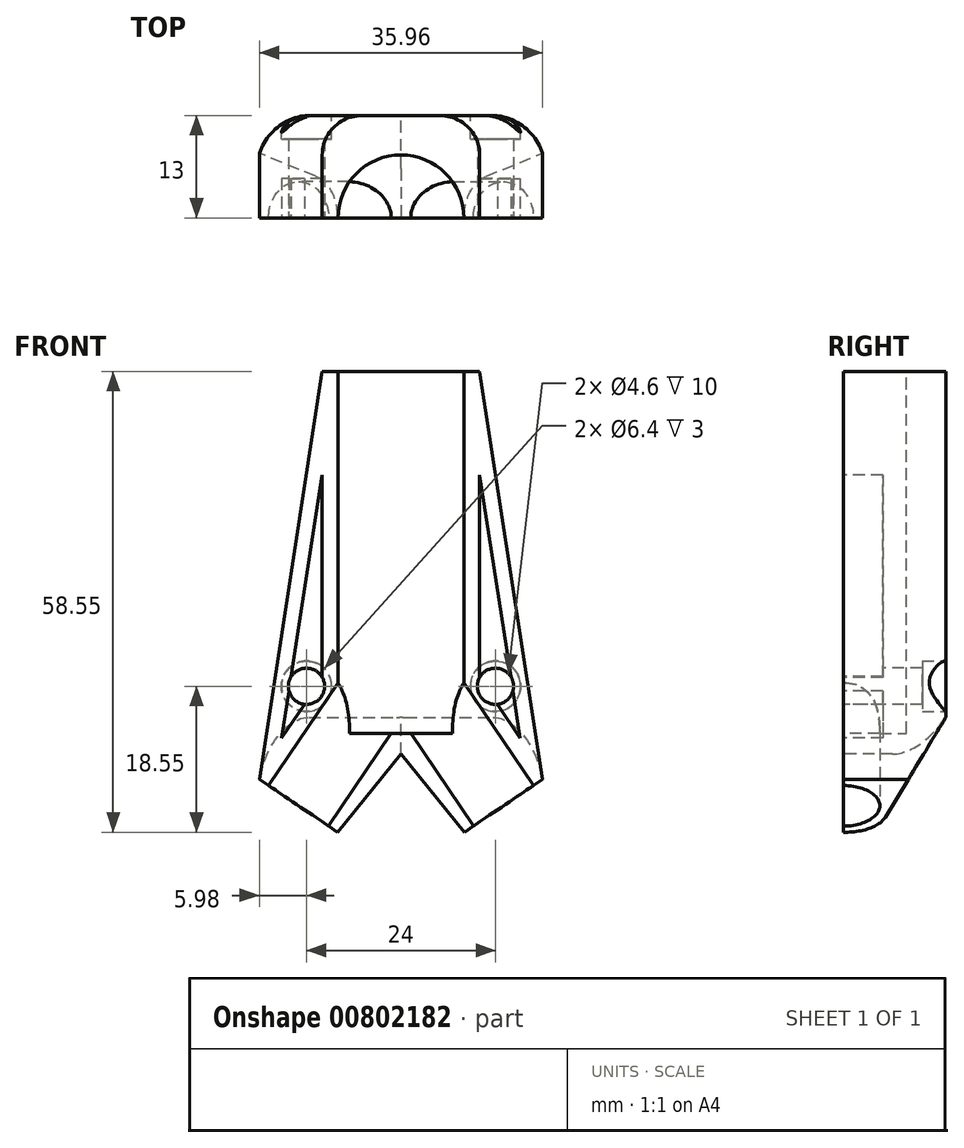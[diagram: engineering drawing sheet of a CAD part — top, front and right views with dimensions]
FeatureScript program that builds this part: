
annotation { "Feature Type Name" : "Feature", "Feature Type Description" : "" }
export const myFeature = defineFeature(function(context is Context, id is Id, definition is map)
    precondition{}
    {
        {
            var Q0;
            Q0=qCreatedBy(makeId("Front.planeOp"),FACE);
            var sketch = newSketch(context, id + "F0", { "sketchPlane" : qUnion([Q0])});
            skLineSegment(sketch, "E0", {"start": v(0, 0) * mm, "end": v(0, 0) * mm});
            skLineSegment(sketch, "E1.bottom", {"start": v(-10, 40) * mm, "end": v(10, 40) * mm});
            skLineSegment(sketch, "E2", {"start": v(0, -8.61) * mm, "end": v(-8.04, -18.55) * mm});
            skLineSegment(sketch, "E3", {"start": v(-8.04, -18.55) * mm, "end": v(-17.98, -11.83) * mm});
            skLineSegment(sketch, "E4", {"start": v(0, 54.25) * mm, "end": v(0, -48.28) * mm, "construction": true});
            skLineSegment(sketch, "E5.MirrorCS", {"start": v(0, -8.61) * mm, "end": v(8.04, -18.55) * mm});
            skLineSegment(sketch, "E6.MirrorCS", {"start": v(8.04, -18.55) * mm, "end": v(17.98, -11.83) * mm});
            skLineSegment(sketch, "E7", {"start": v(-10, 40) * mm, "end": v(-17.98, -11.83) * mm});
            skLineSegment(sketch, "E8", {"start": v(10, 40) * mm, "end": v(17.98, -11.83) * mm});
            skPoint(sketch, "E9.MirrorCS.start.orphan", {"position": v(10, 0) * mm});
            skLineSegment(sketch, "E10", {"start": v(-10, 40) * mm, "end": v(-10, 0) * mm, "construction": true});
            skLineSegment(sketch, "E11", {"start": v(-10, 0) * mm, "end": v(-17.98, -11.83) * mm, "construction": true});
            skLineSegment(sketch, "E12", {"start": v(10, 40) * mm, "end": v(10, 0) * mm, "construction": true});
            skLineSegment(sketch, "E13", {"start": v(10, 0) * mm, "end": v(17.98, -11.83) * mm, "construction": true});
            skLineSegment(sketch, "E14", {"start": v(-10, 0) * mm, "end": v(10, 0) * mm, "construction": true});
            skCircle(sketch, "E15", {"center": v(-12, 0) * mm, "radius": 2.3 * mm});
            skCircle(sketch, "E16.MirrorC", {"center": v(12, 0) * mm, "radius": 2.3 * mm});
            skLineSegment(sketch, "E17", {"start": v(0, 0) * mm, "end": v(13, -15.2) * mm, "construction": true});
            skSolve(sketch);
        }
        {
            var Q0;
            Q0=makeQuery(id+"F0.imprint","IMPRINT",FACE,{"disambiguationData":[TD([[makeQuery(id+"F0.imprint","IMPRINT",EDGE,{"derivedFrom":sQuery(id+"F0.wireOp",EDGE,"E1.bottom")}),-1.0]])]});
            var Q1;
            Q1=makeQuery(id+"F0.imprint","IMPRINT",FACE,{"disambiguationData":[TD([[makeQuery(id+"F0.imprint","IMPRINT",EDGE,{"derivedFrom":sQuery(id+"F0.wireOp",EDGE,"E1.top")}),-1.0]])]});
            extrude(context, id + "F1", {"entities" : qUnion([Q0, Q1]), "oppositeDirection" : true, "depth" : 13 * mm, "offsetDistance" : 25 * mm});
        }
        {
            var Q0;
            Q0=makeQuery(id+"F1.opExtrude","SWEPT_FACE",FACE,{"disambiguationData":[OSD([sQuery(id+"F0.wireOp",EDGE,"E1.bottom")])]});
            var sketch = newSketch(context, id + "F2", { "sketchPlane" : qUnion([Q0])});
            skCircle(sketch, "E18", {"center": v(0, 0) * mm, "radius": 8 * mm});
            skSolve(sketch);
        }
        {
            var Q0;
            {var subQ0=sQuery(id+"F2.wireOp",EDGE,"E18");var subQ1=makeQuery(id+"F1.opExtrude","CAP_EDGE",EDGE,{"disambiguationData":[OSD([sQuery(id+"F0.wireOp",EDGE,"E1.bottom")])],"isStart":true});var subQ2=makeQuery(id+"F2.imprint","INTERSECT",VERTEX,{"disambiguationData":[OD(0.0)],"derivedFrom":[subQ1,subQ0]});Q0=makeQuery(id+"F2.imprint","IMPRINT",FACE,{"disambiguationData":[TD([[makeQuery(id+"F2.imprint","IMPRINT",EDGE,{"disambiguationData":[TD([[subQ2,1.0]])],"derivedFrom":subQ0}),1.0]])]});}
            extrude(context, id + "F3", {"entities" : qUnion([Q0]), "operationType" : NewBodyOperationType.REMOVE, "oppositeDirection" : true, "depth" : 46 * mm, "offsetDistance" : 25 * mm});
        }
        {
            var Q0;
            Q0=qCreatedBy(makeId("Right.planeOp"),FACE);
            cPlane(context, id + "F4", {"entities" : qUnion([Q0]), "cplaneType" : CPlaneType.OFFSET, "offset" : 25 * mm, "width" : 150 * mm, "height" : 150 * mm});
        }
        {
            var Q0;
            Q0=qCreatedBy(id+"F4.planeOp",FACE);
            var sketch = newSketch(context, id + "F5", { "sketchPlane" : qUnion([Q0])});
            skLineSegment(sketch, "E19", {"start": v(4.14, -18.55) * mm, "end": v(13, -18.55) * mm});
            skLineSegment(sketch, "E20", {"start": v(13, -3.95) * mm, "end": v(13, -18.55) * mm});
            skLineSegment(sketch, "E21", {"start": v(4.14, -18.55) * mm, "end": v(13, -3.95) * mm});
            skSolve(sketch);
        }
        {
            var Q0;
            Q0 = qSketchRegion(id + "F5", true);
            extrude(context, id + "F6", {"entities" : qUnion([Q0]), "operationType" : NewBodyOperationType.REMOVE, "oppositeDirection" : true, "depth" : 52.2 * mm, "offsetDistance" : 25 * mm});
        }
        {
            var Q0;
            Q0=makeQuery(id+"F1.opExtrude","SWEPT_FACE",FACE,{"disambiguationData":[OSD([sQuery(id+"F0.wireOp",EDGE,"E3")])]});
            var sketch = newSketch(context, id + "F7", { "sketchPlane" : qUnion([Q0])});
            skCircle(sketch, "E22", {"center": v(-2.28, 0) * mm, "radius": 4.6 * mm});
            skSolve(sketch);
        }
        {
            var Q0;
            {var subQ0=sQuery(id+"F7.wireOp",EDGE,"E22");var subQ1=makeQuery(id+"F1.opExtrude","CAP_EDGE",EDGE,{"disambiguationData":[OSD([sQuery(id+"F0.wireOp",EDGE,"E3")])],"isStart":true});var subQ2=makeQuery(id+"F7.imprint","INTERSECT",VERTEX,{"disambiguationData":[OD(0.0)],"derivedFrom":[subQ1,subQ0]});Q0=makeQuery(id+"F7.imprint","IMPRINT",FACE,{"disambiguationData":[TD([[makeQuery(id+"F7.imprint","IMPRINT",EDGE,{"disambiguationData":[TD([[subQ2,1.0]])],"derivedFrom":subQ0}),1.0]])]});}
            extrude(context, id + "F8", {"entities" : qUnion([Q0]), "operationType" : NewBodyOperationType.REMOVE, "oppositeDirection" : true, "depth" : 25 * mm, "offsetDistance" : 25 * mm});
        }
        {
            var Q0;
            Q0=makeQuery(id+"F1.opExtrude","SWEPT_FACE",FACE,{"disambiguationData":[OSD([sQuery(id+"F0.wireOp",EDGE,"E6.MirrorCS")])]});
            var sketch = newSketch(context, id + "F9", { "sketchPlane" : qUnion([Q0])});
            skCircle(sketch, "E23", {"center": v(2.28, 0) * mm, "radius": 4.6 * mm});
            skSolve(sketch);
        }
        {
            var Q0;
            {var subQ0=sQuery(id+"F9.wireOp",EDGE,"E23");var subQ1=makeQuery(id+"F1.opExtrude","CAP_EDGE",EDGE,{"disambiguationData":[OSD([sQuery(id+"F0.wireOp",EDGE,"E6.MirrorCS")])],"isStart":true});var subQ2=makeQuery(id+"F9.imprint","INTERSECT",VERTEX,{"disambiguationData":[OD(0.0)],"derivedFrom":[subQ1,subQ0]});Q0=makeQuery(id+"F9.imprint","IMPRINT",FACE,{"disambiguationData":[TD([[makeQuery(id+"F9.imprint","IMPRINT",EDGE,{"disambiguationData":[TD([[subQ2,-1.0]])],"derivedFrom":subQ0}),1.0]])]});}
            extrude(context, id + "F10", {"entities" : qUnion([Q0]), "operationType" : NewBodyOperationType.REMOVE, "oppositeDirection" : true, "depth" : 25 * mm, "offsetDistance" : 25 * mm});
        }
        {
            var Q0;
            Q0=makeQuery(id+"F1.opExtrude","CAP_EDGE",EDGE,{"disambiguationData":[OSD([sQuery(id+"F0.wireOp",EDGE,"E7")])],"isStart":false});
            var Q1;
            Q1=makeQuery(id+"F1.opExtrude","CAP_EDGE",EDGE,{"disambiguationData":[OSD([sQuery(id+"F0.wireOp",EDGE,"E8")])],"isStart":false});
            var Q2;
            Q2=makeQuery(id+"F6.boolean.opBoolean","INTERSECT",EDGE,{"derivedFrom":[makeQuery(id+"F1.opExtrude","SWEPT_FACE",FACE,{"disambiguationData":[OSD([sQuery(id+"F0.wireOp",EDGE,"E2")])]}),makeQuery(id+"F6.opExtrude","SWEPT_FACE",FACE,{"disambiguationData":[OSD([sQuery(id+"F5.wireOp",EDGE,"E21")])]})]});
            var Q3;
            Q3=makeQuery(id+"F6.boolean.opBoolean","INTERSECT",EDGE,{"derivedFrom":[makeQuery(id+"F1.opExtrude","SWEPT_FACE",FACE,{"disambiguationData":[OSD([sQuery(id+"F0.wireOp",EDGE,"E5.MirrorCS")])]}),makeQuery(id+"F6.opExtrude","SWEPT_FACE",FACE,{"disambiguationData":[OSD([sQuery(id+"F5.wireOp",EDGE,"E21")])]})]});
            fillet(context, id + "F11", {"entities" : qUnion([Q0, Q1, Q2, Q3]), "radius" : 5 * mm, "tangentPropagation" : true, "allowEdgeOverflow" : false});
        }
        {
            var Q0;
            {var subQ0=sQuery(id+"F0.wireOp",EDGE,"E8");var subQ2=sQuery(id+"F0.wireOp",EDGE,"E6.MirrorCS");var subQ4=sQuery(id+"F0.wireOp",EDGE,"E16.MirrorC");var subQ6=sQuery(id+"F0.wireOp",EDGE,"E1.bottom");var subQ7=makeQuery(id+"F1.opExtrude","SWEPT_FACE",FACE,{"disambiguationData":[OSD([subQ6])]});var subQ10=sQuery(id+"F0.wireOp",EDGE,"E3");var subQ11=sQuery(id+"F0.wireOp",EDGE,"E2");var subQ12=sQuery(id+"F0.wireOp",EDGE,"E5.MirrorCS");Q0=makeQuery(id+"F10.boolean.opBoolean","SPLIT",FACE,{"disambiguationData":[TD([subQ7])],"derivedFrom":makeQuery(id+"F8.boolean.opBoolean","SPLIT",FACE,{"disambiguationData":[TD([makeQuery(id+"F1.opExtrude","SWEPT_FACE",FACE,{"disambiguationData":[OSD([subQ11])]})])],"derivedFrom":makeQuery(id+"F1.opExtrude","CAP_FACE",FACE,{"disambiguationData":[OSD([subQ6,subQ11,subQ10,subQ12,subQ2,sQuery(id+"F0.wireOp",EDGE,"E7"),subQ0,sQuery(id+"F0.wireOp",EDGE,"E15"),subQ4])],"isStart":true})})});}
            var sketch = newSketch(context, id + "F12", { "sketchPlane" : qUnion([Q0])});
            skLineSegment(sketch, "E24.0", {"start": v(10, 26.86) * mm, "end": v(15.15, -6.56) * mm});
            skLineSegment(sketch, "E24.1", {"start": v(10, 1.05) * mm, "end": v(10, 26.86) * mm});
            skLineSegment(sketch, "E24.2", {"start": v(10, 1.05) * mm, "end": v(15.15, -6.56) * mm});
            skSolve(sketch);
        }
        {
            var Q0;
            {var subQ0=sQuery(id+"F0.wireOp",EDGE,"E7");var subQ1=sQuery(id+"F0.wireOp",EDGE,"E15");var subQ2=sQuery(id+"F0.wireOp",EDGE,"E3");var subQ3=sQuery(id+"F0.wireOp",EDGE,"E1.bottom");Q0=makeQuery(id+"F8.boolean.opBoolean","SPLIT",FACE,{"disambiguationData":[TD([makeQuery(id+"F1.opExtrude","SWEPT_FACE",FACE,{"disambiguationData":[OSD([subQ0])]})])],"derivedFrom":makeQuery(id+"F1.opExtrude","CAP_FACE",FACE,{"disambiguationData":[OSD([subQ3,sQuery(id+"F0.wireOp",EDGE,"E2"),subQ2,sQuery(id+"F0.wireOp",EDGE,"E5.MirrorCS"),sQuery(id+"F0.wireOp",EDGE,"E6.MirrorCS"),subQ0,sQuery(id+"F0.wireOp",EDGE,"E8"),subQ1,sQuery(id+"F0.wireOp",EDGE,"E16.MirrorC")])],"isStart":true})});}
            var sketch = newSketch(context, id + "F13", { "sketchPlane" : qUnion([Q0])});
            skSolve(sketch);
        }
        {
            var Q0;
            {var subQ6=sQuery(id+"F0.wireOp",EDGE,"E7");Q0=makeQuery(id+"F13.imprint","IMPRINT",FACE,{"disambiguationData":[TD([[makeQuery(id+"F13.imprint","IMPRINT",EDGE,{"derivedFrom":makeQuery(id+"F1.opExtrude","CAP_EDGE",EDGE,{"disambiguationData":[OSD([subQ6])],"isStart":true})}),1.0]])]});}
            var sketch = newSketch(context, id + "F14", { "sketchPlane" : qUnion([Q0])});
            skLineSegment(sketch, "E25.0", {"start": v(-10, 1.05) * mm, "end": v(-10, 26.86) * mm});
            skLineSegment(sketch, "E25.1", {"start": v(-10, 1.05) * mm, "end": v(-15.15, -6.56) * mm});
            skLineSegment(sketch, "E25.2", {"start": v(-10, 26.86) * mm, "end": v(-15.15, -6.56) * mm});
            skSolve(sketch);
        }
        {
            var Q0;
            Q0 = qSketchRegion(id + "F14", true);
            extrude(context, id + "F15", {"entities" : qUnion([Q0]), "operationType" : NewBodyOperationType.REMOVE, "oppositeDirection" : true, "depth" : 5 * mm, "offsetDistance" : 25 * mm});
        }
        {
            var Q0;
            Q0 = qSketchRegion(id + "F12", true);
            extrude(context, id + "F16", {"entities" : qUnion([Q0]), "operationType" : NewBodyOperationType.REMOVE, "oppositeDirection" : true, "depth" : 5 * mm, "offsetDistance" : 25 * mm});
        }
        {
            var Q0;
            Q0=makeQuery(id+"F1.opExtrude","CAP_FACE",FACE,{"disambiguationData":[OSD([sQuery(id+"F0.wireOp",EDGE,"E1.bottom"),sQuery(id+"F0.wireOp",EDGE,"E2"),sQuery(id+"F0.wireOp",EDGE,"E3"),sQuery(id+"F0.wireOp",EDGE,"E5.MirrorCS"),sQuery(id+"F0.wireOp",EDGE,"E6.MirrorCS"),sQuery(id+"F0.wireOp",EDGE,"E7"),sQuery(id+"F0.wireOp",EDGE,"E8"),sQuery(id+"F0.wireOp",EDGE,"E15"),sQuery(id+"F0.wireOp",EDGE,"E16.MirrorC")])],"isStart":false});
            cPlane(context, id + "F17", {"entities" : qUnion([Q0]), "cplaneType" : CPlaneType.OFFSET, "offset" : 25 * mm, "width" : 150 * mm, "height" : 150 * mm});
        }
        {
            var Q0;
            Q0=qCreatedBy(id+"F17.planeOp",FACE);
            var sketch = newSketch(context, id + "F18", { "sketchPlane" : qUnion([Q0])});
            skCircle(sketch, "E26", {"center": v(-12, 0) * mm, "radius": 3.2 * mm});
            skCircle(sketch, "E27", {"center": v(12, 0) * mm, "radius": 3.2 * mm});
            skSolve(sketch);
        }
        {
            var Q0;
            Q0=makeQuery(id+"F18.imprint","IMPRINT",FACE,{"disambiguationData":[TD([[makeQuery(id+"F18.imprint","IMPRINT",EDGE,{"derivedFrom":sQuery(id+"F18.wireOp",EDGE,"E26")}),1.0]])]});
            var Q1;
            Q1=makeQuery(id+"F18.imprint","IMPRINT",FACE,{"disambiguationData":[TD([[makeQuery(id+"F18.imprint","IMPRINT",EDGE,{"derivedFrom":sQuery(id+"F18.wireOp",EDGE,"E27")}),1.0]])]});
            extrude(context, id + "F19", {"entities" : qUnion([Q0, Q1]), "operationType" : NewBodyOperationType.REMOVE, "oppositeDirection" : true, "depth" : 28 * mm, "offsetDistance" : 25 * mm});
        }
    });
